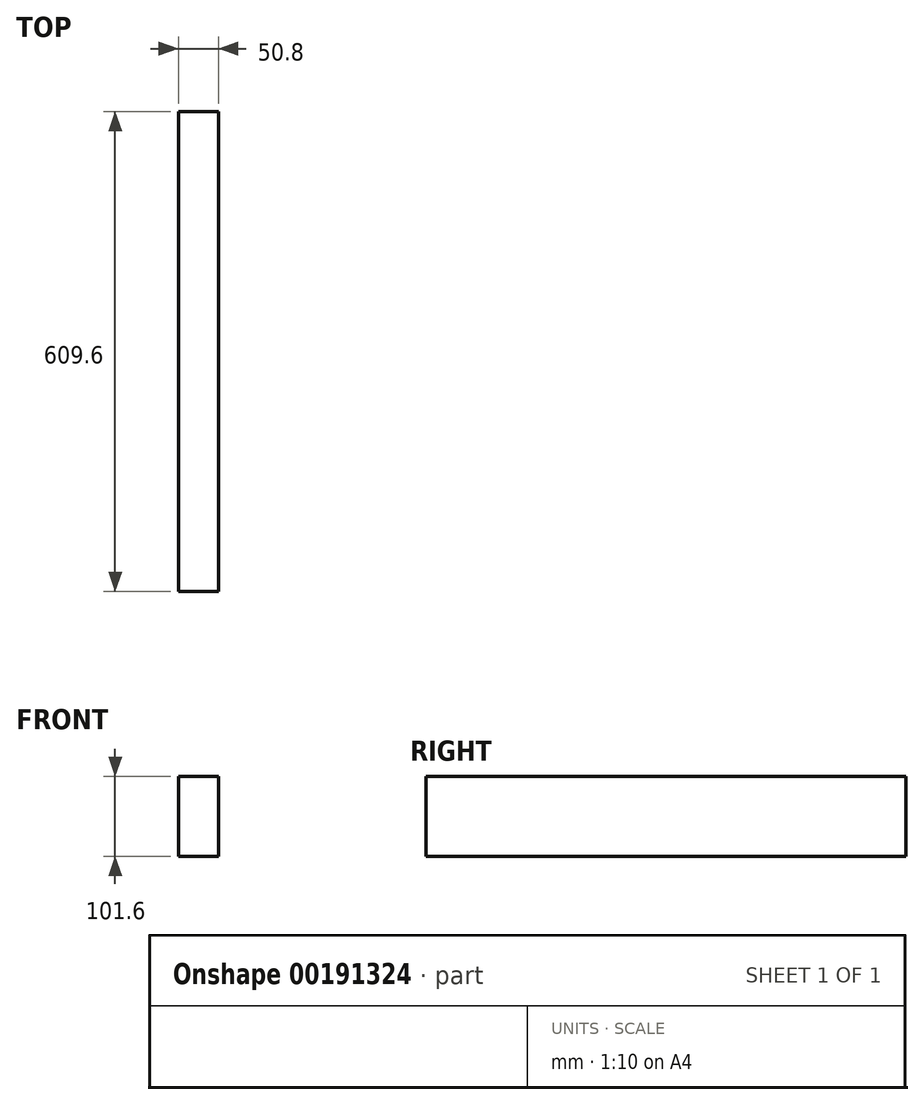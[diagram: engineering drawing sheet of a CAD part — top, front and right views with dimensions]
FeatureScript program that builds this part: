
annotation { "Feature Type Name" : "Feature", "Feature Type Description" : "" }
export const myFeature = defineFeature(function(context is Context, id is Id, definition is map)
    precondition{}
    {
        {
            var Q0;
            Q0=qCreatedBy(makeId("Front.planeOp"),FACE);
            var sketch = newSketch(context, id + "F0", { "sketchPlane" : qUnion([Q0])});
            skLineSegment(sketch, "E0.bottom", {"start": v(-25.4, 50.8) * mm, "end": v(25.4, 50.8) * mm});
            skLineSegment(sketch, "E0.top", {"start": v(-25.4, -50.8) * mm, "end": v(25.4, -50.8) * mm});
            skLineSegment(sketch, "E0.left", {"start": v(-25.4, 50.8) * mm, "end": v(-25.4, -50.8) * mm});
            skLineSegment(sketch, "E0.right", {"start": v(25.4, 50.8) * mm, "end": v(25.4, -50.8) * mm});
            skLineSegment(sketch, "E1", {"start": v(-25.4, 50.8) * mm, "end": v(25.4, -50.8) * mm, "construction": true});
            skSolve(sketch);
        }
        {
            var Q0;
            Q0=makeQuery(id+"F0.imprint","IMPRINT",FACE,{"disambiguationData":[TD([[makeQuery(id+"F0.imprint","IMPRINT",EDGE,{"derivedFrom":sQuery(id+"F0.wireOp",EDGE,"E0.bottom")}),-1.0]])]});
            extrude(context, id + "F1", {"entities" : qUnion([Q0]), "depth" : 609.6 * mm});
        }
    });
